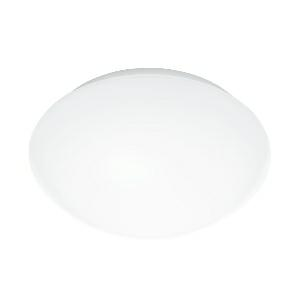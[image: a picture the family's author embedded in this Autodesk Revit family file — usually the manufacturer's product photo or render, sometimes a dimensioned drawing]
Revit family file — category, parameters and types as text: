
# Revit family: rs_pro_led_p1_056032
name_source: partatom
category: Leuchten
revit_build: Autodesk Revit 2016 (Build: 20190508_0715(x64)
units: mm (PartAtom-declared; Revit-internal decimal feet)

## family parameters
Basisbauteil = Fläche
Beim Laden mit Abzugskörper schneiden = Nein
Bemaßung runder Anschluss = Durchmesser verwenden
Gemeinsam genutzt = Nein
Lichtquelle = Nein
Raumberechnungspunkt = Nein
Teiletyp = Normal

## types (1)
- RS PRO LED P1 (1 x , 1010 lm, 4000 K)
    Beschreibung = Dimensions (Ø x H): 280 x 110 mm; Mains power supply: 220 – 240 V / 50 – 60 Hz; Sensor Technology: High frequency; Transmitter power: < 1 mW; HF-system: 5,8 GHz; Output: 9,5 W; Interconnection: Yes; Type of interconnection: Master/master; Luminous flux: 1010 lm; Colour temperature: 4000 K; Colour variation LED: SDCM3; Colour Rendering Index CRI: 80-89; With lamp: Yes, STEINEL LED system; Lamp: LED cannot be replaced; LED life expectancy (max. °C): 50000 h; Drop in luminous flux in accordance with LM80: L80B10; Base: without; LED cooling system: Passive Thermo Control; With motion detector: Yes; Detection: also through glass, wood and stud walls; Detection angle: 360 °; Angle of aperture: 160 °; Capability of masking out individual segments: Yes; Electronic scalability: Yes; Mechanical scalability: No; Reach, radial: Ø 8 m (50 m²); Reach, tangential: Ø 8 m (50 m²); Continuous light: selectable, 4h; Photo-cell controller: Yes; Twilight setting: 2 – 2000 lx; Time setting: 5 sec – 15 min; Basic light level function: Yes; Basic light level function time: 10/30 min, all night; Soft light start: Yes; Impact resistance: IK03; IP-rating: IP54; Protection class: II; Ambient temperature: 10 – 40 °C; Housing material: Plastic; Cover material: Plastic, opal; Manufacturer's Warranty: 5 years; Settings via: Potentiometers; With remote control: No; Version: Neutral white; PU1, EAN: 4007841056032
    CIE Flux Codes = 41 70 89 89 100
    Color Rendering = 80-89
    Color Temperature = 4000 K
    Frequency = 60 Hz, 50 Hz
    Height = 0 mm  [stored 0 ft]
    Hersteller = Steinel
    Lamp Light Flux = 1010 lm
    Lamp count = 1
    Lampe = 1 x
    Length = 280 mm
    Luminous efficacy = 112 lm/W
    ModVariant = Nein
    Modell = 056032
    Mounting Type = Surface mounted
    Number of Poles = 1
    OnlyDefault = Ja
    Power Factor = 1
    Product Name = RS PRO LED P1
    Product group = Sensor-switched indoor light
    ProductGroupID = 30
    Protection Class = Protection class II
    Protection Degree = IP 54
    RlxData = <blob elided: 62625 chars, md5=2c031827>
    Scheinlast = 9 VA
    Socket = socket
    Standby Power = 0 W
    System Light Flux = 1010 lm
    System Power = 9 W
    Typenbild = produkt1_056032.jpg
    Typenkommentare = Product without accessories
    URL = http://relux.com
    VarID = ---
    Voltage = 0 V
    Vorgabe-Ansicht = 1800 mm
    Weight = 0.00 kg
    Width = 0 mm  [stored 0 ft]

note: [stored X ft] marks values corroborated as IEEE doubles in the binary element streams (Revit-internal decimal feet)

## geometry (parser evidence)
native form markers: Blend x4, Sweep x14
no freeform markers — native parametric forms only
